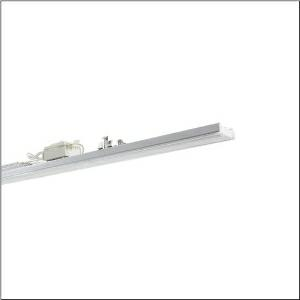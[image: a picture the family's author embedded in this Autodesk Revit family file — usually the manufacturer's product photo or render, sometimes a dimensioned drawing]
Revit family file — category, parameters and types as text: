
# Revit family: licross_r__11_recessed_mo_51tl11de45xg_4314
name_source: partatom
category: Lighting Fixtures
units: mm (PartAtom-declared; Revit-internal decimal feet)

## family parameters
Cut with Voids When Loaded = No
Host = Face
Light Source = No
Part Type = Normal
Room Calculation Point = No
Round Connector Dimension = Use Diameter
Shared = No

## types (1)
- --- (1 x LED, 5040 lm, 29.6 W, 4000K)
    Apparent Load = 30 VA
    CIE Flux Codes = 89 96 99 100 100
    Color Rendering = 80
    Color Temperature = 4000K
    Default Elevation = 1800 mm
    Description = Licross® 11 Recessed MO, luminaire insert, of sheet steel, coil coated, white, length: 750mm, width: 66mm, height: 67mm, LED rated luminous flux: 5.040lm, light colour: 840, control gear: DALI 2, with plug, 5-pole, with phase selection, mains connection: 220..240V, AC, 50/60Hz, rated input power: 30W, halogen-free wiring, primary light control with lens, of plastic, primary optical cover: cover, of PMMA, light emission: direct distribution, primary light characteristic: symmetric, protection rating (complete): IP40, insulation class (complete): insulation class I (protective earthing), certification: CE, ENEC, VDE, UKCA, protection symbol: D if used in an environment without relevant dust loads with corresponding accessories, impact resistance: IK06, permissible ambient temperature for indoor applications: -25..+35°C, corresponds to IFS (International Featured Standards) requirements for safety and quality in the food industry, reducing of maximum allowable ambient temperature of 5°C with ceiling mounting, LABS conformity tested according to VDMA 24364:2018-05, packaging unit: 1 piece
    Height = 58 mm
    Lamp = 1 x LED
    Lamp Light Flux = 5040 lm
    Lamp Power = 29.6 W
    Lamp count = 1
    Length = 750 mm
    Luminous efficacy = 170 lm/W
    Manufacturer = Siteco
    ModVariant = No
    Model = 51TL11DE45XG
    Mounting Place = Ceiling
    Mounting Type = Pendant
    Number of Poles = 1
    OnlyDefault = Yes
    Power Factor = 1
    Product Name = Licross® 11 Recessed MO
    Product group = luminaire insert
    ProductGroupID = 902
    Protection Class = Protection class I
    Protection Degree = IP 40
    RLX_Detail_Level = 1
    RLX_Emergency_Light_Flux = 0 lm
    RLX_Emergency_Type = 0
    RLX_Emergency_Type_DB = No
    RlxData = <blob elided: 29041 chars, md5=a5679641>
    Socket = socket
    Standby Power = 0 W
    System Light Flux = 5040 lm
    System Power = 30 W
    Type Comments = factory setting: luminous flux: 100 % | dim-lin: 254 | 378 mA
    Type Image = l_1296930.jpg
    URL = http://relux.com
    VarID = @adj_098574
    Voltage = 0 V
    Weight = 0.00 kg
    Width = 66 mm

## geometry (parser evidence)
native form markers: Blend x4, Sweep x11
no freeform markers — native parametric forms only
